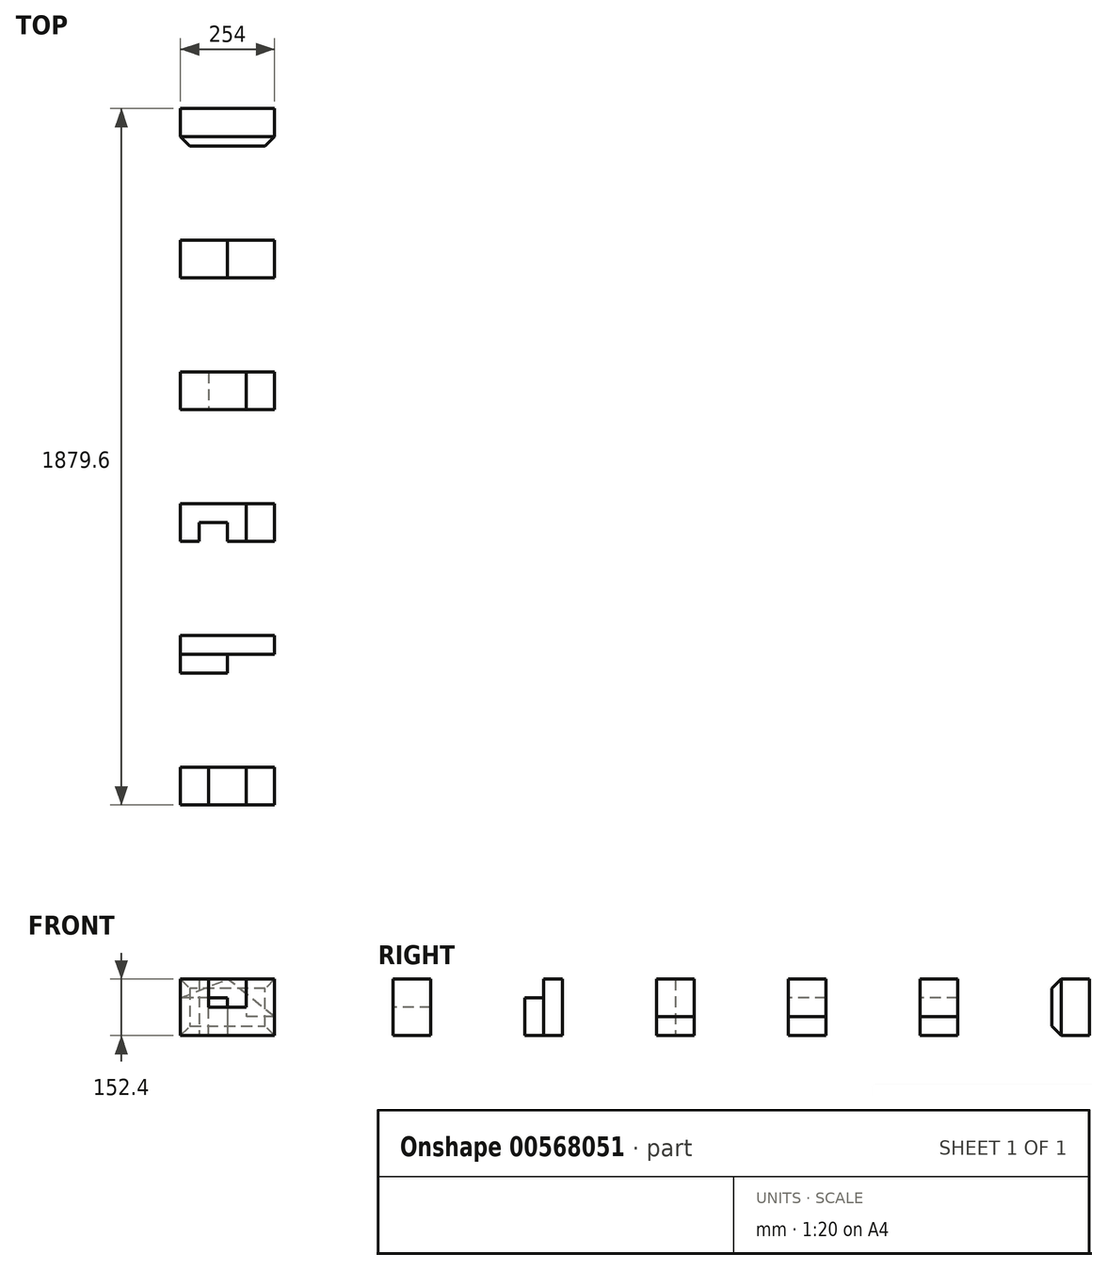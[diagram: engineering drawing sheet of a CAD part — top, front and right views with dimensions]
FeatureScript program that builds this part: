
annotation { "Feature Type Name" : "Feature", "Feature Type Description" : "" }
export const myFeature = defineFeature(function(context is Context, id is Id, definition is map)
    precondition{}
    {
        {
            var Q0;
            Q0=qCreatedBy(makeId("Front.planeOp"),FACE);
            var sketch = newSketch(context, id + "F0", { "sketchPlane" : qUnion([Q0])});
            skLineSegment(sketch, "E0", {"start": v(0, 0) * mm, "end": v(0, 152.4) * mm});
            skLineSegment(sketch, "E1", {"start": v(0, 152.4) * mm, "end": v(76.2, 152.4) * mm});
            skLineSegment(sketch, "E2", {"start": v(76.2, 152.4) * mm, "end": v(76.2, 76.2) * mm});
            skLineSegment(sketch, "E3", {"start": v(76.2, 76.2) * mm, "end": v(177.8, 76.2) * mm});
            skLineSegment(sketch, "E4", {"start": v(177.8, 76.2) * mm, "end": v(177.8, 152.4) * mm});
            skLineSegment(sketch, "E5", {"start": v(177.8, 152.4) * mm, "end": v(254, 152.4) * mm});
            skLineSegment(sketch, "E6", {"start": v(254, 152.4) * mm, "end": v(254, 0) * mm});
            skLineSegment(sketch, "E7", {"start": v(254, 0) * mm, "end": v(0, 0) * mm});
            skSolve(sketch);
        }
        {
            var Q0;
            Q0=makeQuery(id+"F0.imprint","IMPRINT",FACE,{"disambiguationData":[TD([[makeQuery(id+"F0.imprint","IMPRINT",EDGE,{"derivedFrom":sQuery(id+"F0.wireOp",EDGE,"E0")}),-1.0]])]});
            extrude(context, id + "F1", {"entities" : qUnion([Q0]), "oppositeDirection" : true, "depth" : 101.6 * mm, "offsetDistance" : 25.4 * mm});
        }
        {
            var Q0;
            Q0=qCreatedBy(makeId("Right.planeOp"),FACE);
            var sketch = newSketch(context, id + "F2", { "sketchPlane" : qUnion([Q0])});
            skLineSegment(sketch, "E8", {"start": v(355.6, 0) * mm, "end": v(457.2, 0) * mm});
            skLineSegment(sketch, "E9", {"start": v(457.2, 0) * mm, "end": v(457.2, 152.4) * mm});
            skLineSegment(sketch, "E10", {"start": v(457.2, 152.4) * mm, "end": v(406.4, 152.4) * mm});
            skLineSegment(sketch, "E11", {"start": v(406.4, 152.4) * mm, "end": v(406.4, 101.6) * mm});
            skLineSegment(sketch, "E12", {"start": v(406.4, 101.6) * mm, "end": v(355.6, 101.6) * mm});
            skLineSegment(sketch, "E13", {"start": v(355.6, 101.6) * mm, "end": v(355.6, 0) * mm});
            skSolve(sketch);
        }
        {
            var Q0;
            Q0=makeQuery(id+"F2.imprint","IMPRINT",FACE,{"disambiguationData":[TD([[makeQuery(id+"F2.imprint","IMPRINT",EDGE,{"derivedFrom":sQuery(id+"F2.wireOp",EDGE,"E8")}),1.0]])]});
            extrude(context, id + "F3", {"entities" : qUnion([Q0]), "depth" : 254 * mm, "offsetDistance" : 25.4 * mm});
        }
        {
            var Q0;
            Q0=makeQuery(id+"F3.opExtrude","CAP_FACE",FACE,{"disambiguationData":[OSD([sQuery(id+"F2.wireOp",EDGE,"E8"),sQuery(id+"F2.wireOp",EDGE,"E9"),sQuery(id+"F2.wireOp",EDGE,"E10"),sQuery(id+"F2.wireOp",EDGE,"E11"),sQuery(id+"F2.wireOp",EDGE,"E12"),sQuery(id+"F2.wireOp",EDGE,"E13")])],"isStart":false});
            var sketch = newSketch(context, id + "F4", { "sketchPlane" : qUnion([Q0])});
            skLineSegment(sketch, "E14.bottom", {"start": v(355.6, 101.6) * mm, "end": v(406.4, 101.6) * mm});
            skLineSegment(sketch, "E14.top", {"start": v(355.6, 0) * mm, "end": v(406.4, 0) * mm});
            skLineSegment(sketch, "E14.left", {"start": v(355.6, 101.6) * mm, "end": v(355.6, 0) * mm});
            skLineSegment(sketch, "E14.right", {"start": v(406.4, 101.6) * mm, "end": v(406.4, 0) * mm});
            skSolve(sketch);
        }
        {
            var Q0;
            Q0=makeQuery(id+"F4.imprint","IMPRINT",FACE,{"disambiguationData":[TD([[makeQuery(id+"F4.imprint","IMPRINT",EDGE,{"derivedFrom":sQuery(id+"F4.wireOp",EDGE,"E14.bottom")}),1.0]])]});
            extrude(context, id + "F5", {"entities" : qUnion([Q0]), "operationType" : NewBodyOperationType.REMOVE, "oppositeDirection" : true, "depth" : 127 * mm, "offsetDistance" : 25.4 * mm});
        }
        {
            var Q0;
            Q0=qCreatedBy(makeId("Top.planeOp"),FACE);
            var sketch = newSketch(context, id + "F6", { "sketchPlane" : qUnion([Q0])});
            skLineSegment(sketch, "E15", {"start": v(0, 711.2) * mm, "end": v(50.8, 711.2) * mm});
            skLineSegment(sketch, "E16", {"start": v(50.8, 711.2) * mm, "end": v(50.8, 762) * mm});
            skLineSegment(sketch, "E17", {"start": v(50.8, 762) * mm, "end": v(127, 762) * mm});
            skLineSegment(sketch, "E18", {"start": v(127, 762) * mm, "end": v(127, 711.2) * mm});
            skLineSegment(sketch, "E19", {"start": v(127, 711.2) * mm, "end": v(254, 711.2) * mm});
            skLineSegment(sketch, "E20", {"start": v(254, 711.2) * mm, "end": v(254, 812.8) * mm});
            skLineSegment(sketch, "E21", {"start": v(254, 812.8) * mm, "end": v(0, 812.8) * mm});
            skLineSegment(sketch, "E22", {"start": v(0, 812.8) * mm, "end": v(0, 711.2) * mm});
            skSolve(sketch);
        }
        {
            var Q0;
            Q0=makeQuery(id+"F6.imprint","IMPRINT",FACE,{"disambiguationData":[TD([[makeQuery(id+"F6.imprint","IMPRINT",EDGE,{"derivedFrom":sQuery(id+"F6.wireOp",EDGE,"E15")}),1.0]])]});
            extrude(context, id + "F7", {"entities" : qUnion([Q0]), "depth" : 152.4 * mm, "offsetDistance" : 25.4 * mm});
        }
        {
            var Q0;
            Q0=makeQuery(id+"F7.opExtrude","SWEPT_FACE",FACE,{"disambiguationData":[OSD([sQuery(id+"F6.wireOp",EDGE,"E19")])]});
            var sketch = newSketch(context, id + "F8", { "sketchPlane" : qUnion([Q0])});
            skLineSegment(sketch, "E23", {"start": v(254, 152.4) * mm, "end": v(177.8, 152.4) * mm});
            skLineSegment(sketch, "E24", {"start": v(177.8, 152.4) * mm, "end": v(177.8, 50.8) * mm});
            skLineSegment(sketch, "E25", {"start": v(177.8, 50.8) * mm, "end": v(254, 50.8) * mm});
            skLineSegment(sketch, "E26", {"start": v(254, 50.8) * mm, "end": v(254, 152.4) * mm});
            skSolve(sketch);
        }
        {
            var Q0;
            Q0=makeQuery(id+"F8.imprint","IMPRINT",FACE,{"disambiguationData":[TD([[makeQuery(id+"F8.imprint","IMPRINT",EDGE,{"derivedFrom":sQuery(id+"F8.wireOp",EDGE,"E23")}),-1.0]])]});
            extrude(context, id + "F9", {"entities" : qUnion([Q0]), "operationType" : NewBodyOperationType.REMOVE, "oppositeDirection" : true, "depth" : 101.6 * mm, "offsetDistance" : 25.4 * mm});
        }
        {
            var Q0;
            Q0=qCreatedBy(makeId("Right.planeOp"),FACE);
            var sketch = newSketch(context, id + "F10", { "sketchPlane" : qUnion([Q0])});
            skLineSegment(sketch, "E27", {"start": v(1066.8, 0) * mm, "end": v(1168.4, 0) * mm});
            skLineSegment(sketch, "E28", {"start": v(1168.4, 0) * mm, "end": v(1168.4, 152.4) * mm});
            skLineSegment(sketch, "E29", {"start": v(1168.4, 152.4) * mm, "end": v(1066.8, 152.4) * mm});
            skLineSegment(sketch, "E30", {"start": v(1066.8, 152.4) * mm, "end": v(1066.8, 0) * mm});
            skSolve(sketch);
        }
        {
            var Q0;
            Q0=makeQuery(id+"F10.imprint","IMPRINT",FACE,{"disambiguationData":[TD([[makeQuery(id+"F10.imprint","IMPRINT",EDGE,{"derivedFrom":sQuery(id+"F10.wireOp",EDGE,"E27")}),1.0]])]});
            extrude(context, id + "F11", {"entities" : qUnion([Q0]), "depth" : 254 * mm, "offsetDistance" : 25.4 * mm});
        }
        {
            var Q0;
            Q0=makeQuery(id+"F11.opExtrude","SWEPT_FACE",FACE,{"disambiguationData":[OSD([sQuery(id+"F10.wireOp",EDGE,"E30")])]});
            var sketch = newSketch(context, id + "F12", { "sketchPlane" : qUnion([Q0])});
            skLineSegment(sketch, "E31.bottom", {"start": v(254, 152.4) * mm, "end": v(177.8, 152.4) * mm});
            skLineSegment(sketch, "E31.top", {"start": v(254, 50.8) * mm, "end": v(177.8, 50.8) * mm});
            skLineSegment(sketch, "E31.left", {"start": v(254, 152.4) * mm, "end": v(254, 50.8) * mm});
            skLineSegment(sketch, "E31.right", {"start": v(177.8, 152.4) * mm, "end": v(177.8, 50.8) * mm});
            skSolve(sketch);
        }
        {
            var Q0;
            Q0=makeQuery(id+"F12.imprint","IMPRINT",FACE,{"disambiguationData":[TD([[makeQuery(id+"F12.imprint","IMPRINT",EDGE,{"derivedFrom":sQuery(id+"F12.wireOp",EDGE,"E31.bottom")}),1.0]])]});
            extrude(context, id + "F13", {"entities" : qUnion([Q0]), "operationType" : NewBodyOperationType.REMOVE, "oppositeDirection" : true, "depth" : 101.6 * mm, "offsetDistance" : 25.4 * mm});
        }
        {
            var Q0;
            Q0=makeQuery(id+"F11.opExtrude","SWEPT_FACE",FACE,{"disambiguationData":[OSD([sQuery(id+"F10.wireOp",EDGE,"E30")])]});
            var sketch = newSketch(context, id + "F14", { "sketchPlane" : qUnion([Q0])});
            skLineSegment(sketch, "E32.bottom", {"start": v(0, 0) * mm, "end": v(76.2, 0) * mm});
            skLineSegment(sketch, "E32.top", {"start": v(0, 101.6) * mm, "end": v(76.2, 101.6) * mm});
            skLineSegment(sketch, "E32.left", {"start": v(0, 0) * mm, "end": v(0, 101.6) * mm});
            skLineSegment(sketch, "E32.right", {"start": v(76.2, 0) * mm, "end": v(76.2, 101.6) * mm});
            skSolve(sketch);
        }
        {
            var Q0;
            Q0=makeQuery(id+"F14.imprint","IMPRINT",FACE,{"disambiguationData":[TD([[makeQuery(id+"F14.imprint","IMPRINT",EDGE,{"derivedFrom":sQuery(id+"F14.wireOp",EDGE,"E32.bottom")}),-1.0]])]});
            extrude(context, id + "F15", {"entities" : qUnion([Q0]), "operationType" : NewBodyOperationType.REMOVE, "oppositeDirection" : true, "depth" : 101.6 * mm, "offsetDistance" : 25.4 * mm});
        }
        {
            var Q0;
            Q0=qCreatedBy(makeId("Right.planeOp"),FACE);
            var sketch = newSketch(context, id + "F16", { "sketchPlane" : qUnion([Q0])});
            skLineSegment(sketch, "E33", {"start": v(1422.4, 0) * mm, "end": v(1524, 0) * mm});
            skLineSegment(sketch, "E34", {"start": v(1524, 0) * mm, "end": v(1524, 152.4) * mm});
            skLineSegment(sketch, "E35", {"start": v(1524, 152.4) * mm, "end": v(1422.4, 152.4) * mm});
            skLineSegment(sketch, "E36", {"start": v(1422.4, 152.4) * mm, "end": v(1422.4, 0) * mm});
            skSolve(sketch);
        }
        {
            var Q0;
            Q0=makeQuery(id+"F16.imprint","IMPRINT",FACE,{"disambiguationData":[TD([[makeQuery(id+"F16.imprint","IMPRINT",EDGE,{"derivedFrom":sQuery(id+"F16.wireOp",EDGE,"E33")}),1.0]])]});
            extrude(context, id + "F17", {"entities" : qUnion([Q0]), "depth" : 254 * mm, "offsetDistance" : 25.4 * mm});
        }
        {
            var Q0;
            Q0=makeQuery(id+"F17.opExtrude","SWEPT_FACE",FACE,{"disambiguationData":[OSD([sQuery(id+"F16.wireOp",EDGE,"E36")])]});
            var sketch = newSketch(context, id + "F18", { "sketchPlane" : qUnion([Q0])});
            skLineSegment(sketch, "E37", {"start": v(254, 50.8) * mm, "end": v(127, 152.4) * mm});
            skLineSegment(sketch, "E38", {"start": v(127, 152.4) * mm, "end": v(254, 152.4) * mm});
            skLineSegment(sketch, "E39", {"start": v(254, 152.4) * mm, "end": v(254, 50.8) * mm});
            skSolve(sketch);
        }
        {
            var Q0;
            Q0=makeQuery(id+"F18.imprint","IMPRINT",FACE,{"disambiguationData":[TD([[makeQuery(id+"F18.imprint","IMPRINT",EDGE,{"derivedFrom":sQuery(id+"F18.wireOp",EDGE,"E37")}),-1.0]])]});
            extrude(context, id + "F19", {"entities" : qUnion([Q0]), "operationType" : NewBodyOperationType.REMOVE, "oppositeDirection" : true, "depth" : 101.6 * mm, "offsetDistance" : 25.4 * mm});
        }
        {
            var Q0;
            Q0=makeQuery(id+"F17.opExtrude","SWEPT_FACE",FACE,{"disambiguationData":[OSD([sQuery(id+"F16.wireOp",EDGE,"E36")])]});
            var sketch = newSketch(context, id + "F20", { "sketchPlane" : qUnion([Q0])});
            skLineSegment(sketch, "E40.left", {"start": v(0, 152.4) * mm, "end": v(0, 101.6) * mm});
            skLineSegment(sketch, "E41", {"start": v(0, 101.6) * mm, "end": v(127, 152.4) * mm});
            skSolve(sketch);
        }
        {
            var Q0;
            Q0=makeQuery(id+"F20.imprint","IMPRINT",FACE,{"disambiguationData":[TD([[makeQuery(id+"F20.imprint","IMPRINT",EDGE,{"derivedFrom":sQuery(id+"F20.wireOp",EDGE,"E40.left")}),1.0]])]});
            extrude(context, id + "F21", {"entities" : qUnion([Q0]), "operationType" : NewBodyOperationType.REMOVE, "oppositeDirection" : true, "depth" : 101.6 * mm, "offsetDistance" : 25.4 * mm});
        }
        {
            var Q0;
            Q0=qCreatedBy(makeId("Right.planeOp"),FACE);
            var sketch = newSketch(context, id + "F22", { "sketchPlane" : qUnion([Q0])});
            skLineSegment(sketch, "E42.bottom", {"start": v(1778, 0) * mm, "end": v(1879.6, 0) * mm});
            skLineSegment(sketch, "E42.top", {"start": v(1778, 152.4) * mm, "end": v(1879.6, 152.4) * mm});
            skLineSegment(sketch, "E42.left", {"start": v(1778, 0) * mm, "end": v(1778, 152.4) * mm});
            skLineSegment(sketch, "E42.right", {"start": v(1879.6, 0) * mm, "end": v(1879.6, 152.4) * mm});
            skSolve(sketch);
        }
        {
            var Q0;
            Q0=makeQuery(id+"F22.imprint","IMPRINT",FACE,{"disambiguationData":[TD([[makeQuery(id+"F22.imprint","IMPRINT",EDGE,{"derivedFrom":sQuery(id+"F22.wireOp",EDGE,"E42.bottom")}),1.0]])]});
            extrude(context, id + "F23", {"entities" : qUnion([Q0]), "depth" : 254 * mm, "offsetDistance" : 25.4 * mm});
        }
        {
            var Q0;
            Q0=makeQuery(id+"F23.opExtrude","SWEPT_FACE",FACE,{"disambiguationData":[OSD([sQuery(id+"F22.wireOp",EDGE,"E42.left")])]});
            chamfer(context, id + "F24", {"entities" : qUnion([Q0]), "width" : 25.4 * mm, "tangentPropagation" : true});
        }
    });
